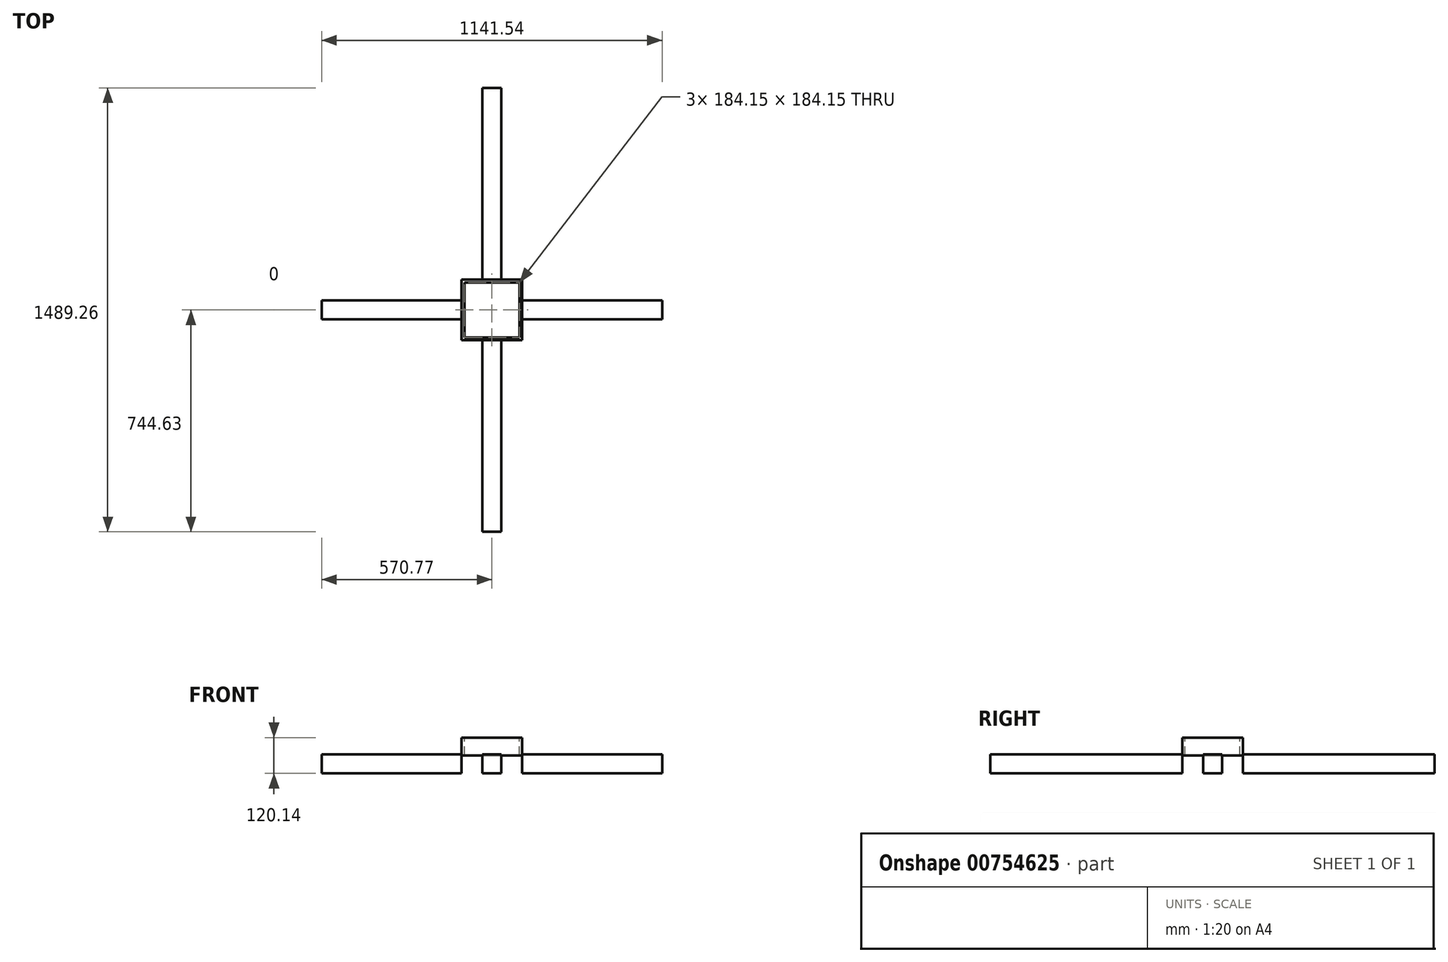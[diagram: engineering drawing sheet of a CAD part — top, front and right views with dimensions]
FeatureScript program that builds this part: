
annotation { "Feature Type Name" : "Feature", "Feature Type Description" : "" }
export const myFeature = defineFeature(function(context is Context, id is Id, definition is map)
    precondition{}
    {
        {
            var Q0;
            Q0=qCreatedBy(makeId("Top.planeOp"),FACE);
            cPlane(context, id + "F0", {"entities" : qUnion([Q0]), "cplaneType" : CPlaneType.OFFSET, "offset" : 76.2 * mm, "oppositeDirection" : true, "width" : 152.4 * mm, "height" : 152.4 * mm});
        }
        {
            var Q0;
            Q0=qCreatedBy(id+"F0.planeOp",FACE);
            var sketch = newSketch(context, id + "F1", { "sketchPlane" : qUnion([Q0])});
            skLineSegment(sketch, "E0.bottom", {"start": v(-101.6, -101.6) * mm, "end": v(101.6, -101.6) * mm});
            skLineSegment(sketch, "E0.top", {"start": v(-101.6, 101.6) * mm, "end": v(101.6, 101.6) * mm});
            skLineSegment(sketch, "E0.left", {"start": v(-101.6, -101.6) * mm, "end": v(-101.6, 101.6) * mm});
            skLineSegment(sketch, "E0.right", {"start": v(101.6, -101.6) * mm, "end": v(101.6, 101.6) * mm});
            skLineSegment(sketch, "E1.0", {"start": v(-92.07, -92.08) * mm, "end": v(-92.08, 92.08) * mm});
            skLineSegment(sketch, "E1.1", {"start": v(-92.07, -92.08) * mm, "end": v(92.08, -92.08) * mm});
            skLineSegment(sketch, "E1.2", {"start": v(92.08, -92.08) * mm, "end": v(92.07, 92.07) * mm});
            skLineSegment(sketch, "E1.3", {"start": v(-92.08, 92.08) * mm, "end": v(92.07, 92.08) * mm});
            skSolve(sketch);
        }
        {
            var Q0;
            Q0=qSketchRegion(id+"F1",true);
            extrude(context, id + "F2", {"entities" : qUnion([Q0]), "oppositeDirection" : true, "depth" : (5 - (2.73 - .5)) * mm, "offsetDistance" : 25.4 * mm, "hasSecondDirection" : true, "secondDirectionOppositeDirection" : false, "secondDirectionDepth" : 56.64 * mm});
        }
        {
            var Q0;
            Q0=qCreatedBy(id+"F0.planeOp",FACE);
            var sketch = newSketch(context, id + "F3", { "sketchPlane" : qUnion([Q0])});
            skLineSegment(sketch, "E2", {"start": v(0, 0) * mm, "end": v(781.72, 0) * mm, "construction": true});
            skLineSegment(sketch, "E3.0", {"start": v(101.6, -31.75) * mm, "end": v(570.77, -31.75) * mm});
            skLineSegment(sketch, "E4.0", {"start": v(101.6, 31.75) * mm, "end": v(570.77, 31.75) * mm});
            skLineSegment(sketch, "E5", {"start": v(0, 0) * mm, "end": v(0, -31.75) * mm});
            skLineSegment(sketch, "E6.0", {"start": v(101.6, 31.75) * mm, "end": v(101.6, -31.75) * mm});
            skLineSegment(sketch, "E7.0", {"start": v(570.77, 31.75) * mm, "end": v(570.77, -31.75) * mm});
            skPoint(sketch, "E8.center", {"position": v(-140.54, 0) * mm});
            skSolve(sketch);
        }
        {
            var Q0;
            Q0=qCreatedBy(makeId("Front.planeOp"),FACE);
            var sketch = newSketch(context, id + "F4", { "sketchPlane" : qUnion([Q0])});
            skLineSegment(sketch, "E9", {"start": v(0, 0) * mm, "end": v(0, -39) * mm, "construction": true});
            skSolve(sketch);
        }
        {
            var Q0;
            Q0=qSketchRegion(id+"F3",true);
            extrude(context, id + "F5", {"entities" : qUnion([Q0]), "oppositeDirection" : true, "depth" : 63.5 * mm, "offsetDistance" : 25.4 * mm});
        }
        {
            var Q0;
            Q0=makeQuery(id+"F5.opExtrude","SWEPT_BODY",BODY,{"disambiguationData":[OSD([sQuery(id+"F3.wireOp",EDGE,"E3.0"),sQuery(id+"F3.wireOp",EDGE,"E4.0"),sQuery(id+"F3.wireOp",EDGE,"E6.0"),sQuery(id+"F3.wireOp",EDGE,"E7.0")])]});
            var Q1;
            Q1=sQuery(id+"F4.wireOp",EDGE,"E9");
            circularPattern(context, id + "F6", {"entities" : qUnion([Q0]), "axis" : qUnion([Q1]), "angle" : 360 * degree, "instanceCount" : 4, "equalSpace" : true});
        }
        {
            var Q0;
            Q0=makeQuery(id+"F6.opPattern","COPY",FACE,{"derivedFrom":makeQuery(id+"F5.opExtrude","SWEPT_FACE",FACE,{"disambiguationData":[OSD([sQuery(id+"F3.wireOp",EDGE,"E7.0")])]}),"instanceName":"3"});
            var sketch = newSketch(context, id + "F7", { "sketchPlane" : qUnion([Q0])});
            skLineSegment(sketch, "E10.bottom", {"start": v(-31.75, -139.7) * mm, "end": v(31.75, -139.7) * mm});
            skLineSegment(sketch, "E10.top", {"start": v(-31.75, -76.2) * mm, "end": v(31.75, -76.2) * mm});
            skLineSegment(sketch, "E10.left", {"start": v(-31.75, -139.7) * mm, "end": v(-31.75, -76.2) * mm});
            skLineSegment(sketch, "E10.right", {"start": v(31.75, -139.7) * mm, "end": v(31.75, -76.2) * mm});
            skSolve(sketch);
        }
        {
            var Q0;
            Q0 = qSketchRegion(id + "F7", true);
            extrude(context, id + "F8", {"entities" : qUnion([Q0]), "operationType" : NewBodyOperationType.ADD, "depth" : 173.86 * mm, "offsetDistance" : 25.4 * mm});
        }
        {
            var Q0;
            Q0=makeQuery(id+"F6.opPattern","COPY",FACE,{"derivedFrom":makeQuery(id+"F5.opExtrude","SWEPT_FACE",FACE,{"disambiguationData":[OSD([sQuery(id+"F3.wireOp",EDGE,"E7.0")])]}),"instanceName":"1"});
            var sketch = newSketch(context, id + "F9", { "sketchPlane" : qUnion([Q0])});
            skLineSegment(sketch, "E11.bottom", {"start": v(-31.75, -139.7) * mm, "end": v(31.75, -139.7) * mm});
            skLineSegment(sketch, "E11.top", {"start": v(-31.75, -76.2) * mm, "end": v(31.75, -76.2) * mm});
            skLineSegment(sketch, "E11.left", {"start": v(-31.75, -139.7) * mm, "end": v(-31.75, -76.2) * mm});
            skLineSegment(sketch, "E11.right", {"start": v(31.75, -139.7) * mm, "end": v(31.75, -76.2) * mm});
            skSolve(sketch);
        }
        {
            var Q0;
            Q0 = qSketchRegion(id + "F9", true);
            extrude(context, id + "F10", {"entities" : qUnion([Q0]), "operationType" : NewBodyOperationType.ADD, "depth" : 173.86 * mm, "offsetDistance" : 25.4 * mm});
        }
    });
